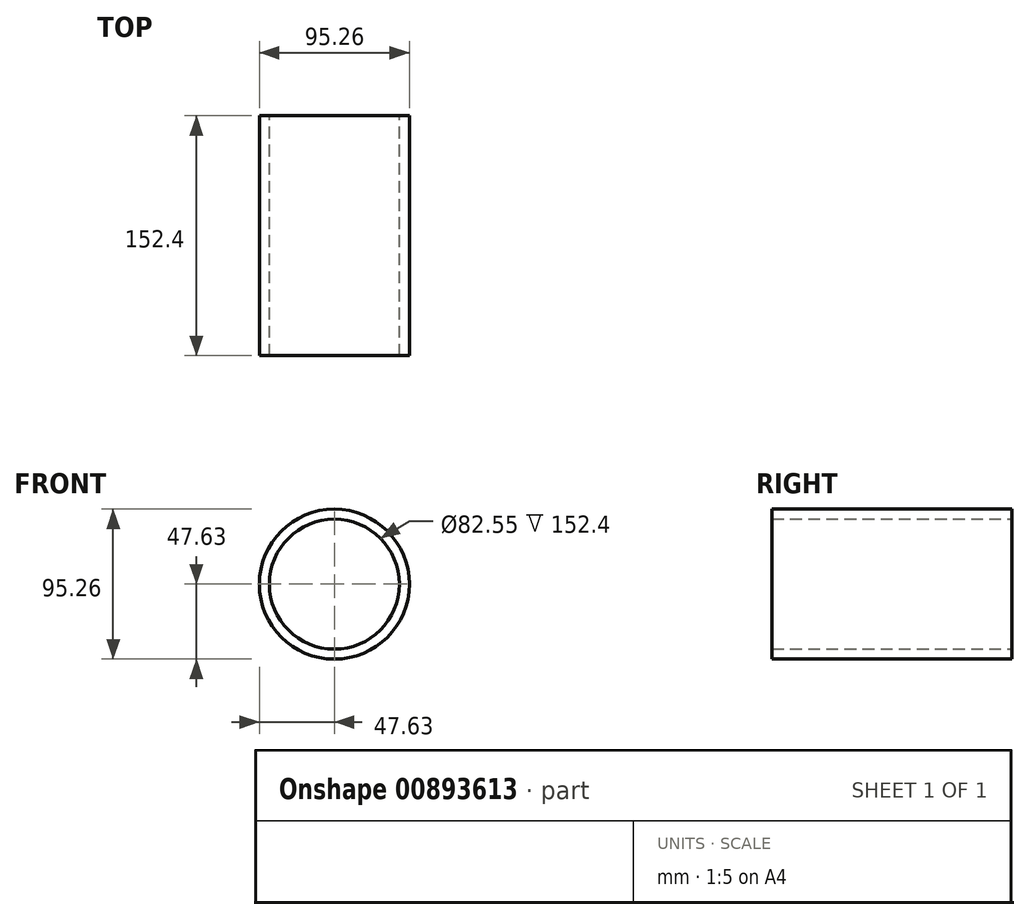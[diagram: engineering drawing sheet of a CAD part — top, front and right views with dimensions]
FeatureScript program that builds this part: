
annotation { "Feature Type Name" : "Feature", "Feature Type Description" : "" }
export const myFeature = defineFeature(function(context is Context, id is Id, definition is map)
    precondition{}
    {
        {
            var Q0;
            Q0=qCreatedBy(makeId("Front.planeOp"),FACE);
            var sketch = newSketch(context, id + "F0", { "sketchPlane" : qUnion([Q0])});
            skCircle(sketch, "E0", {"center": v(0, 0) * mm, "radius": 47.63 * mm});
            skCircle(sketch, "E1.0", {"center": v(0, 0) * mm, "radius": 41.27 * mm});
            skSolve(sketch);
        }
        {
            var Q0;
            Q0=makeQuery(id+"F0.imprint","IMPRINT",FACE,{"disambiguationData":[TD([[makeQuery(id+"F0.imprint","IMPRINT",EDGE,{"derivedFrom":sQuery(id+"F0.wireOp",EDGE,"E0")}),1.0]])]});
            extrude(context, id + "F1", {"entities" : qUnion([Q0]), "endBound" : BoundingType.SYMMETRIC, "depth" : 152.4 * mm, "offsetDistance" : 25.4 * mm});
        }
    });
